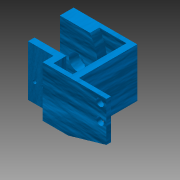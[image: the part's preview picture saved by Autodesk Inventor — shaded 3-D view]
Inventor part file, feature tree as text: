
AUTODESK INVENTOR PART (.ipt)
format: ipt  version: 2015 (Build 190159000, 159)  size: 212,992 bytes
history: native  units: in
note: dims shown in document units (in); Inventor stores cm internally (conversion verified against a paired STEP export)
features: sketch x10, extrude x7, hole x3
ambient origin geometry x8: Origin, YZ Plane, XZ Plane, XY Plane, X Axis, Y Axis, Z Axis, Center Point
bodies: Solid1 (feature_tree)
feature tree (20):
  extrude  "Extrusion1"  Depth=0.9843in
  extrude  "Extrusion2"  Depth=1.0in
  extrude  "Extrusion3"  Depth=1.0in TaperAngle=0.0deg
  hole  "Hole1"  [1 undecoded]
  extrude  "Extrusion4"  Depth=1.3in
  hole  "Hole2"  [1 undecoded]
  extrude  "Extrusion5"  Depth=0.1in
  extrude  "Extrusion6"  Depth=0.6in
  extrude  "Extrusion7"  Depth=0.15in TaperAngle=0.0deg
  hole  "Hole3"  [1 undecoded]
  sketch  "Sketch1"  dims[d1=0.07in d2=0.9843in]
  sketch  "Sketch2"  dims[d3=0.07in d5=1.0in]
  sketch  "Sketch3"  dims[d6=0.1in d7=1.0in d8=0.0in]
  sketch  "Sketch4"  dims[d9=1.9685in d10=0.1457in d11=0.0in]
  sketch  "Sketch5"  dims[d12=0.5079in d13=1.3in]
  sketch  "Sketch6"  dims[d14=3.0in d15=0.0in d16=0.273in]
  sketch  "Sketch7"  dims[d17=0.1in d18=0.2559in]
  sketch  "Sketch8"  dims[d19=0.1181in d20=0.75in d21=0.375in d22=0.25in d23=0.5635in d24=1.0in d25=0.8108in d26=0.6in]
  sketch  "Sketch9"  dims[d28=0.25in d29=0.15in d30=0.0in]
  sketch  "Sketch10"  dims[d31=0.07in d32=0.0591in d33=0.75in d34=0.375in d35=0.25in d36=0.5635in d37=1.0in d38=0.8108in d39=0.4in d40=0.0in d41=0.2in d42=0.0in d43=0.1in d44=0.1in d45=0.4in d46=0.0in d47=0.07in d48=0.33in d49=0.5in d50=0.0591in d51=0.75in d52=0.375in d53=0.25in d54=0.5635in d55=1.0in d56=0.8108in]
note: 3 required parameter values undecoded (feature->parameter linkage not recoverable at this tier; creation-order binding heuristic only, values carry confidence <= 0.55)
